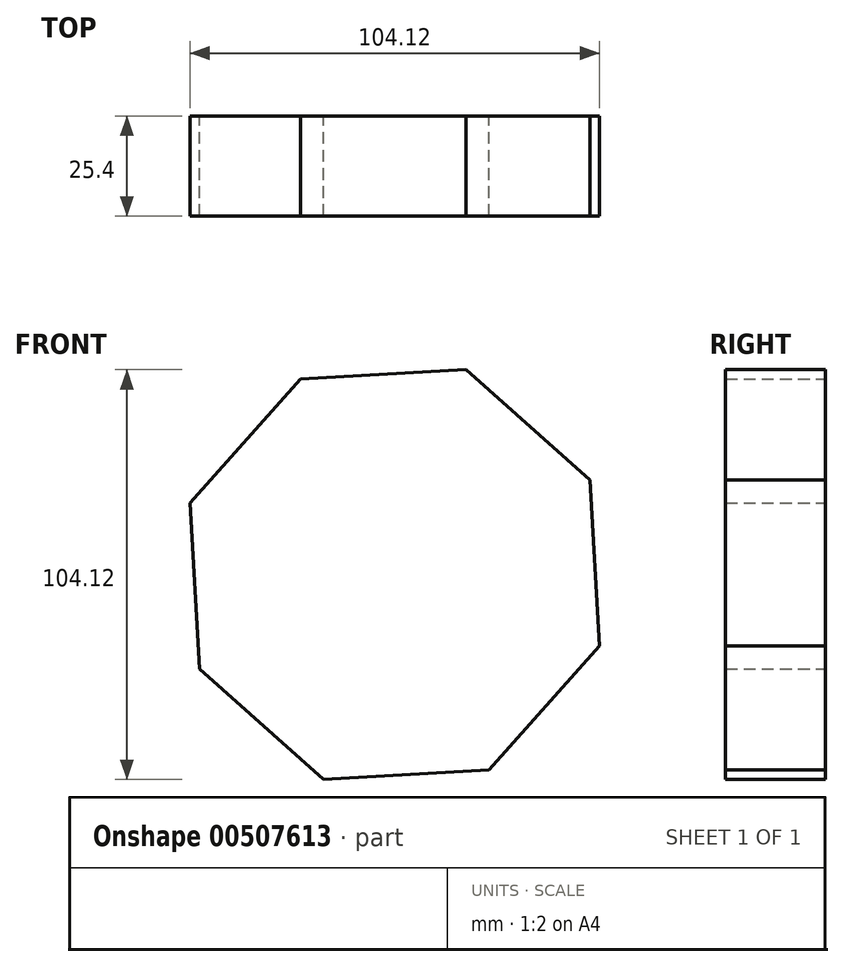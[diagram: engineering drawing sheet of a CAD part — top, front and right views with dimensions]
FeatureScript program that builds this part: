
annotation { "Feature Type Name" : "Feature", "Feature Type Description" : "" }
export const myFeature = defineFeature(function(context is Context, id is Id, definition is map)
    precondition{}
    {
        {
            var Q0;
            Q0=qCreatedBy(makeId("Front.planeOp"),FACE);
            var sketch = newSketch(context, id + "F0", { "sketchPlane" : qUnion([Q0])});
            skCircle(sketch, "E0.cCircle", {"center": v(0, 0) * mm, "radius": 55.13 * mm, "construction": true});
            skLineSegment(sketch, "E0.0", {"start": v(-23.98, 49.64) * mm, "end": v(18.15, 52.06) * mm});
            skLineSegment(sketch, "E0.1", {"start": v(18.15, 52.06) * mm, "end": v(49.64, 23.98) * mm});
            skLineSegment(sketch, "E0.2", {"start": v(49.64, 23.98) * mm, "end": v(52.06, -18.15) * mm});
            skLineSegment(sketch, "E0.3", {"start": v(52.06, -18.15) * mm, "end": v(23.98, -49.64) * mm});
            skLineSegment(sketch, "E0.4", {"start": v(23.98, -49.64) * mm, "end": v(-18.15, -52.06) * mm});
            skLineSegment(sketch, "E0.5", {"start": v(-18.15, -52.06) * mm, "end": v(-49.64, -23.98) * mm});
            skLineSegment(sketch, "E0.6", {"start": v(-49.64, -23.98) * mm, "end": v(-52.06, 18.15) * mm});
            skLineSegment(sketch, "E0.7", {"start": v(-52.06, 18.15) * mm, "end": v(-23.98, 49.64) * mm});
            skSolve(sketch);
        }
        {
            var Q0;
            Q0=makeQuery(id+"F0.imprint","IMPRINT",FACE,{"disambiguationData":[TD([[makeQuery(id+"F0.imprint","IMPRINT",EDGE,{"derivedFrom":sQuery(id+"F0.wireOp",EDGE,"E0.0")}),-1.0]])]});
            extrude(context, id + "F1", {"entities" : qUnion([Q0]), "depth" : 25.4 * mm});
        }
    });
